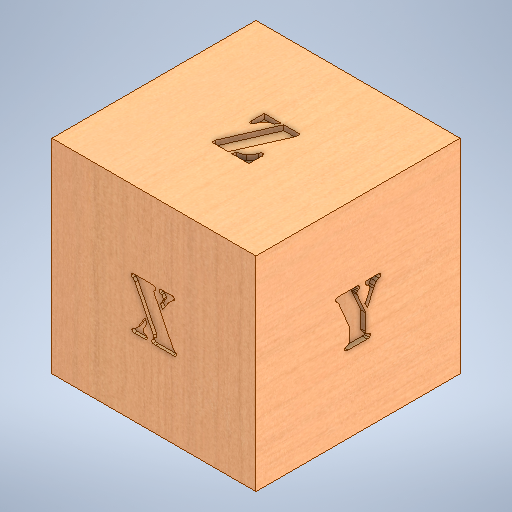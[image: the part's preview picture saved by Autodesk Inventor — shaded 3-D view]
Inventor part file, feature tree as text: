
AUTODESK INVENTOR PART (.ipt)
format: ipt  version: 2025.2 (Build 292293000, 293)  size: 654,336 bytes
history: native  units: mm
features: sketch x12, extrude x4
ambient origin geometry x8: Origin, YZ Plane, XZ Plane, XY Plane, X Axis, Y Axis, Z Axis, Center Point
bodies: Solid1 (feature_tree)
feature tree (16):
  sketch  "Sketch1"  dims[d0=10.0mm d1=50.0mm]
  sketch  "Sketch3"  dims[d11=1200.0mm d13=360.0deg]
  sketch  "Sketch4"  dims[d15=20.0mm d17=10.0mm d18=20.0mm d20=10.0mm]
  sketch  "Sketch5"  dims[d23=200.0mm]
  sketch  "Sketch6"  dims[d24=200.0mm]
  extrude  "Extrusion1"  Depth=50.0mm
  extrude  "Extrusion2"  Depth=50.0mm
  extrude  "Extrusion3"  Depth=50.0mm
  extrude  "Extrusion4"  Depth=60.0mm TaperAngle=360.0deg
  sketch  "Sketch Circular Pattern1"  dims[d2=8.884938mm d3=50.0mm]
  sketch  "Sketch Circular Pattern2"  dims[d6=200.0mm d7=60.0mm d9=360.0deg]
  sketch  "Sketch Rectangular Pattern1"  dims[d4=25.0mm d5=50.0mm]
  sketch  "Sketch7"  dims[d25=0.0mm]
  sketch  "Sketch8"  dims[d26=50.0mm]
  sketch  "Sketch9"  dims[d27=45.616322mm]
  sketch  "Sketch10"  dims[d28=3.0mm d29=0.0mm d30=44.79167mm d31=50.0mm d32=5.0mm d33=0.0mm d34=39.279516mm d35=50.0mm d36=5.0mm d37=0.0mm]
